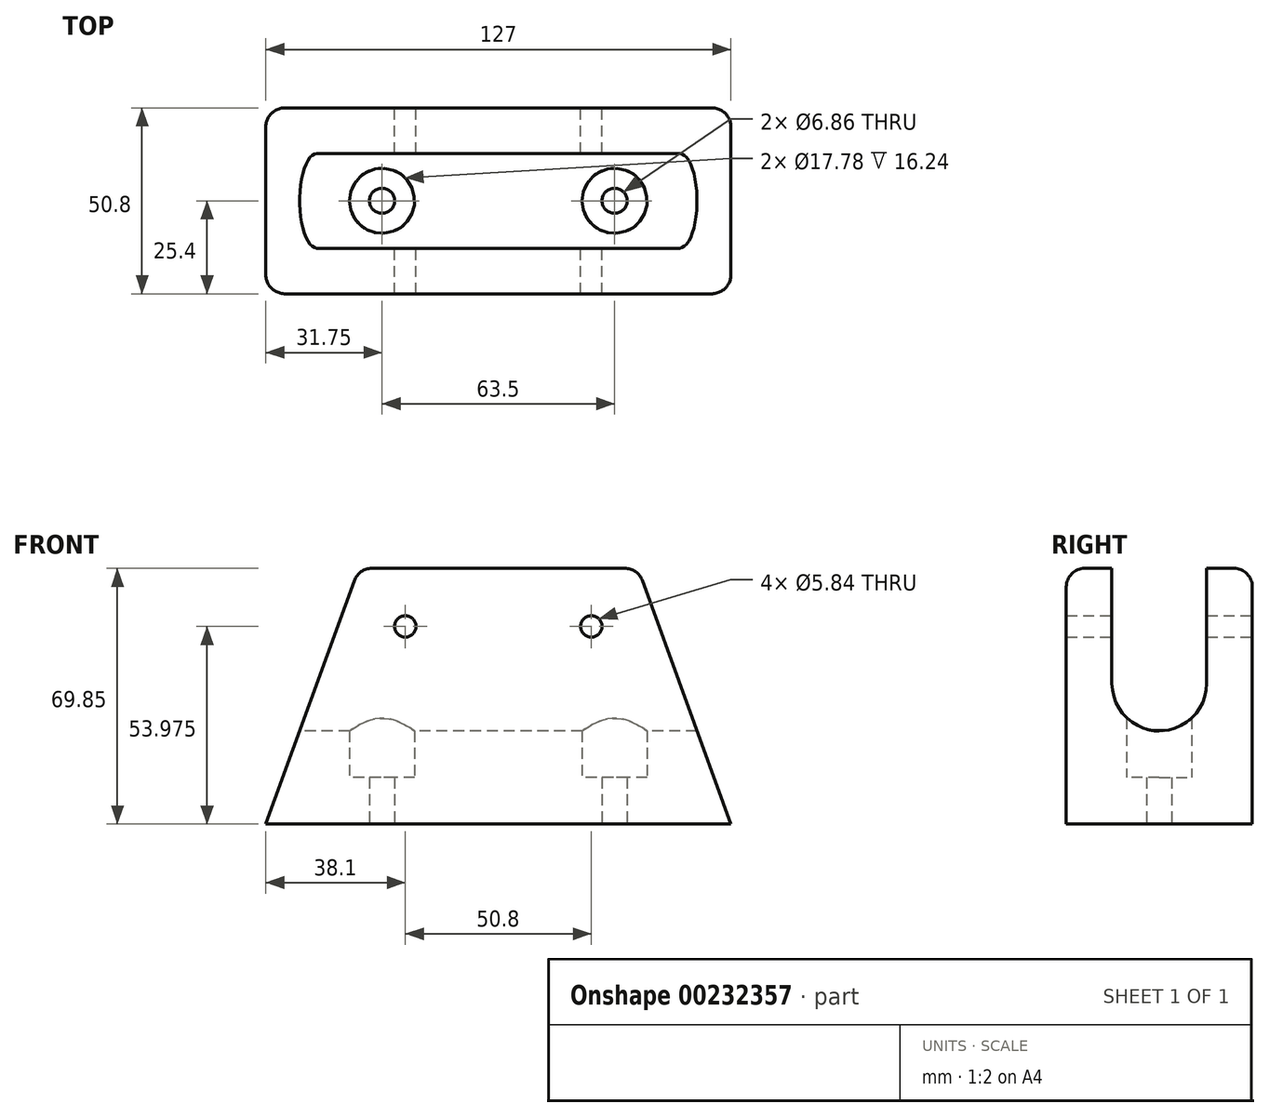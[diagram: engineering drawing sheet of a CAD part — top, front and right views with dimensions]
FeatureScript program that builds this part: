
annotation { "Feature Type Name" : "Feature", "Feature Type Description" : "" }
export const myFeature = defineFeature(function(context is Context, id is Id, definition is map)
    precondition{}
    {
        {
            var Q0;
            Q0=qCreatedBy(makeId("Front.planeOp"),FACE);
            var sketch = newSketch(context, id + "F0", { "sketchPlane" : qUnion([Q0])});
            skLineSegment(sketch, "E0.bottom", {"start": v(0, 0) * mm, "end": v(127, 0) * mm});
            skLineSegment(sketch, "E0.top", {"start": v(25.4, 69.85) * mm, "end": v(101.6, 69.85) * mm});
            skLineSegment(sketch, "E1", {"start": v(25.4, 69.85) * mm, "end": v(0, 0) * mm});
            skLineSegment(sketch, "E2", {"start": v(101.6, 69.85) * mm, "end": v(127, 0) * mm});
            skCircle(sketch, "E3", {"center": v(38.1, 53.98) * mm, "radius": 2.92 * mm});
            skCircle(sketch, "E4", {"center": v(88.9, 53.98) * mm, "radius": 2.92 * mm});
            skSolve(sketch);
        }
        {
            var Q0;
            Q0 = qSketchRegion(id + "F0", true);
            extrude(context, id + "F1", {"entities" : qUnion([Q0]), "depth" : 50.8 * mm});
        }
        {
            var Q0;
            Q0=qCreatedBy(makeId("Right.planeOp"),FACE);
            var sketch = newSketch(context, id + "F2", { "sketchPlane" : qUnion([Q0])});
            skArc(sketch, "E5", {"start": v(-38.35, 38.35) * mm, "mid": v(-25.4, 25.4) * mm, "end": v(-12.45, 38.35) * mm});
            skLineSegment(sketch, "E6", {"start": v(-12.45, 38.35) * mm, "end": v(-12.45, 88.24) * mm});
            skLineSegment(sketch, "E7", {"start": v(-38.35, 38.35) * mm, "end": v(-38.35, 86.91) * mm});
            skLineSegment(sketch, "E8", {"start": v(-38.35, 86.91) * mm, "end": v(-12.45, 88.24) * mm});
            skSolve(sketch);
        }
        {
            var Q0;
            Q0 = qSketchRegion(id + "F2", true);
            extrude(context, id + "F3", {"entities" : qUnion([Q0]), "operationType" : NewBodyOperationType.REMOVE, "depth" : 278.64 * mm});
        }
        {
            var Q0;
            Q0=makeQuery(id+"F1.opExtrude","CAP_EDGE",EDGE,{"disambiguationData":[OSD([sQuery(id+"F0.wireOp",EDGE,"E2")])],"isStart":false});
            var Q1;
            Q1=makeQuery(id+"F1.opExtrude","CAP_EDGE",EDGE,{"disambiguationData":[OSD([sQuery(id+"F0.wireOp",EDGE,"E0.top")])],"isStart":false});
            var Q2;
            Q2=makeQuery(id+"F1.opExtrude","CAP_EDGE",EDGE,{"disambiguationData":[OSD([sQuery(id+"F0.wireOp",EDGE,"E1")])],"isStart":false});
            var Q3;
            {var subQ0=sQuery(id+"F0.wireOp",EDGE,"E2");var subQ1=sQuery(id+"F0.wireOp",EDGE,"E0.top");Q3=makeQuery(id+"F3.boolean.opBoolean","SPLIT",EDGE,{"disambiguationData":[TD([makeQuery(id+"F3.opExtrude","SWEPT_FACE",FACE,{"disambiguationData":[OSD([sQuery(id+"F2.wireOp",EDGE,"E7")])]})])],"derivedFrom":makeQuery(id+"F1.opExtrude","SWEPT_EDGE",EDGE,{"disambiguationData":[OSD([subQ1,subQ0])]})});}
            var Q4;
            {var subQ0=sQuery(id+"F0.wireOp",EDGE,"E1");var subQ1=sQuery(id+"F0.wireOp",EDGE,"E0.top");Q4=makeQuery(id+"F3.boolean.opBoolean","SPLIT",EDGE,{"disambiguationData":[TD([makeQuery(id+"F3.opExtrude","SWEPT_FACE",FACE,{"disambiguationData":[OSD([sQuery(id+"F2.wireOp",EDGE,"E7")])]})])],"derivedFrom":makeQuery(id+"F1.opExtrude","SWEPT_EDGE",EDGE,{"disambiguationData":[OSD([subQ1,subQ0])]})});}
            var Q5;
            {var subQ0=sQuery(id+"F0.wireOp",EDGE,"E1");var subQ1=sQuery(id+"F0.wireOp",EDGE,"E0.top");Q5=makeQuery(id+"F3.boolean.opBoolean","SPLIT",EDGE,{"disambiguationData":[TD([makeQuery(id+"F3.opExtrude","SWEPT_FACE",FACE,{"disambiguationData":[OSD([sQuery(id+"F2.wireOp",EDGE,"E6")])]})])],"derivedFrom":makeQuery(id+"F1.opExtrude","SWEPT_EDGE",EDGE,{"disambiguationData":[OSD([subQ1,subQ0])]})});}
            var Q6;
            Q6=makeQuery(id+"F1.opExtrude","CAP_EDGE",EDGE,{"disambiguationData":[OSD([sQuery(id+"F0.wireOp",EDGE,"E0.top")])],"isStart":true});
            var Q7;
            {var subQ0=sQuery(id+"F0.wireOp",EDGE,"E2");var subQ1=sQuery(id+"F0.wireOp",EDGE,"E0.top");Q7=makeQuery(id+"F3.boolean.opBoolean","SPLIT",EDGE,{"disambiguationData":[TD([makeQuery(id+"F3.opExtrude","SWEPT_FACE",FACE,{"disambiguationData":[OSD([sQuery(id+"F2.wireOp",EDGE,"E6")])]})])],"derivedFrom":makeQuery(id+"F1.opExtrude","SWEPT_EDGE",EDGE,{"disambiguationData":[OSD([subQ1,subQ0])]})});}
            var Q8;
            Q8=makeQuery(id+"F1.opExtrude","CAP_EDGE",EDGE,{"disambiguationData":[OSD([sQuery(id+"F0.wireOp",EDGE,"E2")])],"isStart":true});
            var Q9;
            Q9=makeQuery(id+"F1.opExtrude","CAP_EDGE",EDGE,{"disambiguationData":[OSD([sQuery(id+"F0.wireOp",EDGE,"E1")])],"isStart":true});
            fillet(context, id + "F4", {"entities" : qUnion([Q0, Q1, Q2, Q3, Q4, Q5, Q6, Q7, Q8, Q9]), "radius" : 5.08 * mm, "tangentPropagation" : true, "allowEdgeOverflow" : false});
        }
        {
            var Q0;
            Q0=makeQuery(id+"F1.opExtrude","SWEPT_FACE",FACE,{"disambiguationData":[OSD([sQuery(id+"F0.wireOp",EDGE,"E0.bottom")])]});
            var sketch = newSketch(context, id + "F5", { "sketchPlane" : qUnion([Q0])});
            skLineSegment(sketch, "E9", {"start": v(0, 25.4) * mm, "end": v(63.5, 25.4) * mm});
            skLineSegment(sketch, "E10", {"start": v(63.5, 25.4) * mm, "end": v(31.75, 25.4) * mm});
            skLineSegment(sketch, "E11", {"start": v(31.75, 25.4) * mm, "end": v(95.25, 25.4) * mm});
            skCircle(sketch, "E12", {"center": v(31.75, 25.4) * mm, "radius": 3.43 * mm});
            skCircle(sketch, "E13", {"center": v(95.25, 25.4) * mm, "radius": 3.43 * mm});
            skSolve(sketch);
        }
        {
            var Q0;
            Q0 = qSketchRegion(id + "F5", true);
            extrude(context, id + "F6", {"entities" : qUnion([Q0]), "operationType" : NewBodyOperationType.REMOVE, "oppositeDirection" : true, "depth" : 79.5 * mm});
        }
        {
            var Q0;
            Q0=qCreatedBy(makeId("Top.planeOp"),FACE);
            cPlane(context, id + "F7", {"entities" : qUnion([Q0]), "cplaneType" : CPlaneType.OFFSET, "offset" : 12.7 * mm, "width" : 152.4 * mm, "height" : 152.4 * mm});
        }
        {
            var Q0;
            Q0=qCreatedBy(id+"F7.planeOp",FACE);
            var sketch = newSketch(context, id + "F8", { "sketchPlane" : qUnion([Q0])});
            skLineSegment(sketch, "E14", {"start": v(0, 0) * mm, "end": v(0, -25.4) * mm});
            skLineSegment(sketch, "E15", {"start": v(0, -25.4) * mm, "end": v(31.75, -25.4) * mm});
            skLineSegment(sketch, "E16", {"start": v(31.75, -25.4) * mm, "end": v(95.25, -25.4) * mm});
            skCircle(sketch, "E17", {"center": v(31.75, -25.4) * mm, "radius": 8.9 * mm});
            skCircle(sketch, "E18", {"center": v(95.25, -25.4) * mm, "radius": 8.9 * mm});
            skSolve(sketch);
        }
        {
            var Q0;
            Q0 = qSketchRegion(id + "F8", true);
            extrude(context, id + "F9", {"entities" : qUnion([Q0]), "operationType" : NewBodyOperationType.REMOVE, "depth" : 68.07 * mm});
        }
    });
